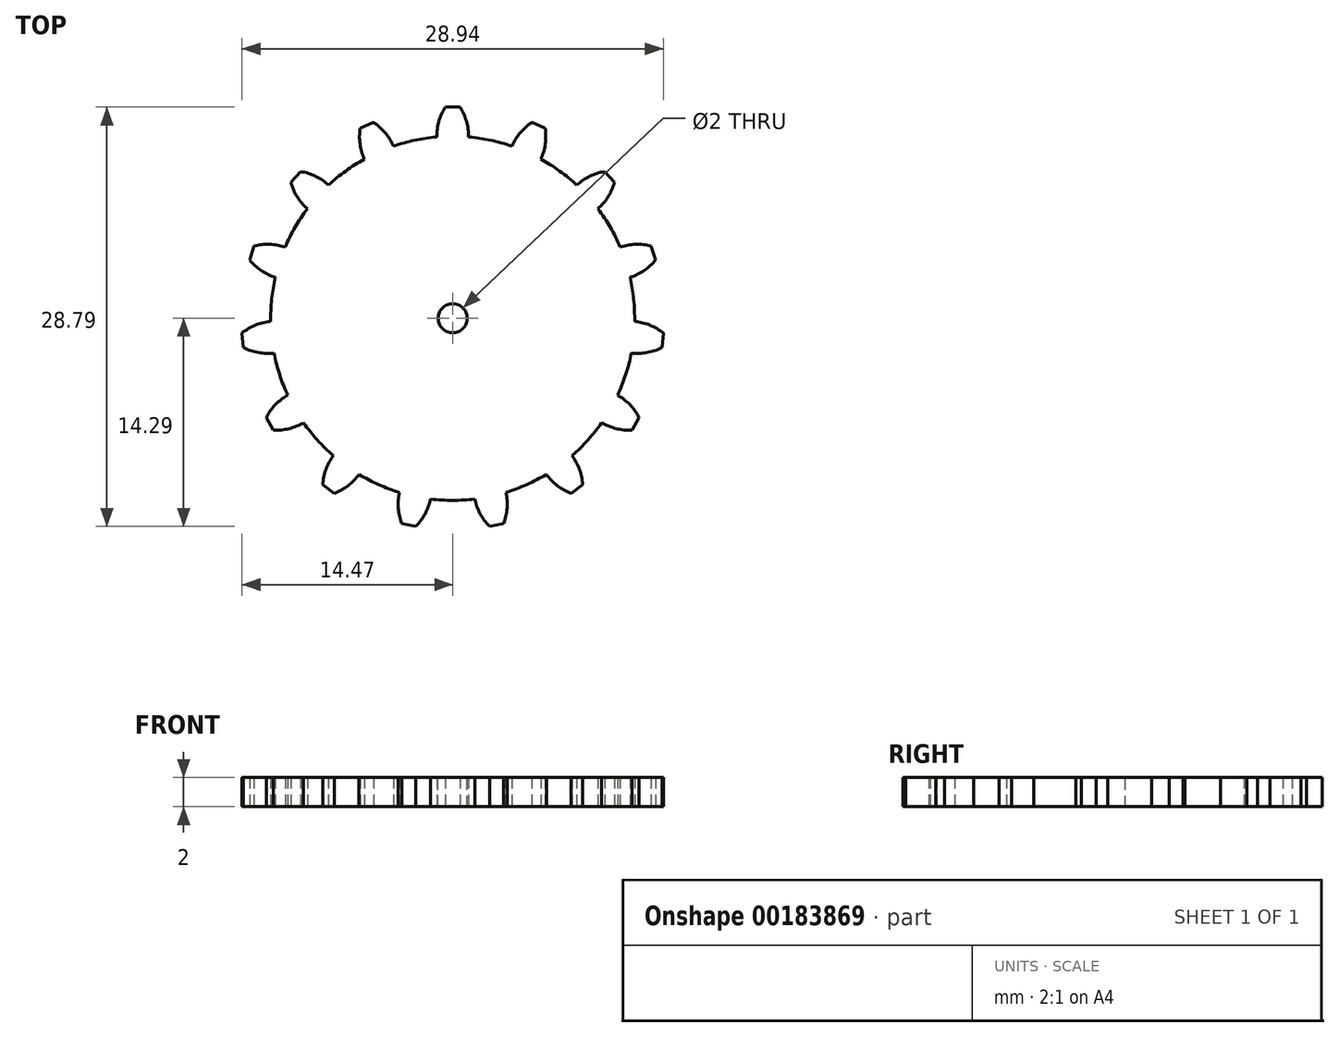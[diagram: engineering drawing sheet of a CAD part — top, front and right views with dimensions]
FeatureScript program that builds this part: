
annotation { "Feature Type Name" : "Feature", "Feature Type Description" : "" }
export const myFeature = defineFeature(function(context is Context, id is Id, definition is map)
    precondition{}
    {
        {
            var Q0;
            Q0=qCreatedBy(makeId("Top.planeOp"),FACE);
            var sketch = newSketch(context, id + "F0", { "sketchPlane" : qUnion([Q0])});
            skCircle(sketch, "E0", {"center": v(0, 0) * mm, "radius": 12.5 * mm});
            skLineSegment(sketch, "E1", {"start": v(0, 0) * mm, "end": v(0, 12.5) * mm, "construction": true});
            skLineSegment(sketch, "E2", {"start": v(0, 14.5) * mm, "end": v(-0.5, 14.5) * mm});
            skArc(sketch, "E3", {"start": v(-0.5, 14.5) * mm, "mid": v(-0.95, 13.52) * mm, "end": v(-1.09, 12.45) * mm});
            skLineSegment(sketch, "E4.MirrorCS", {"start": v(0, 14.5) * mm, "end": v(0.5, 14.5) * mm});
            skArc(sketch, "E5.MirrorCS", {"start": v(0.5, 14.5) * mm, "mid": v(0.95, 13.52) * mm, "end": v(1.09, 12.45) * mm});
            skArc(sketch, "E6.1.0", {"start": v(-6.35, 13.04) * mm, "mid": v(-6.36, 11.97) * mm, "end": v(-6.06, 10.93) * mm});
            skLineSegment(sketch, "E6.1.1", {"start": v(-5.9, 13.25) * mm, "end": v(-6.35, 13.04) * mm});
            skLineSegment(sketch, "E6.1.2", {"start": v(-5.9, 13.25) * mm, "end": v(-5.44, 13.45) * mm});
            skArc(sketch, "E6.1.3", {"start": v(-5.44, 13.45) * mm, "mid": v(-4.64, 12.74) * mm, "end": v(-4.07, 11.82) * mm});
            skArc(sketch, "E6.2.0", {"start": v(-11.11, 9.33) * mm, "mid": v(-10.68, 8.34) * mm, "end": v(-9.98, 7.52) * mm});
            skLineSegment(sketch, "E6.2.1", {"start": v(-10.78, 9.7) * mm, "end": v(-11.11, 9.33) * mm});
            skLineSegment(sketch, "E6.2.2", {"start": v(-10.78, 9.7) * mm, "end": v(-10.44, 10.07) * mm});
            skArc(sketch, "E6.2.3", {"start": v(-10.44, 10.07) * mm, "mid": v(-9.41, 9.75) * mm, "end": v(-8.53, 9.14) * mm});
            skArc(sketch, "E6.3.0", {"start": v(-13.94, 4) * mm, "mid": v(-13.15, 3.28) * mm, "end": v(-12.18, 2.81) * mm});
            skLineSegment(sketch, "E6.3.1", {"start": v(-13.8, 4.48) * mm, "end": v(-13.94, 4) * mm});
            skLineSegment(sketch, "E6.3.2", {"start": v(-13.8, 4.48) * mm, "end": v(-13.64, 4.96) * mm});
            skArc(sketch, "E6.3.3", {"start": v(-13.64, 4.96) * mm, "mid": v(-12.57, 5.08) * mm, "end": v(-11.5, 4.88) * mm});
            skArc(sketch, "E6.4.0", {"start": v(-14.37, -2.01) * mm, "mid": v(-13.35, -2.35) * mm, "end": v(-12.27, -2.38) * mm});
            skLineSegment(sketch, "E6.4.1", {"start": v(-14.42, -1.52) * mm, "end": v(-14.37, -2.01) * mm});
            skLineSegment(sketch, "E6.4.2", {"start": v(-14.42, -1.52) * mm, "end": v(-14.47, -1.02) * mm});
            skArc(sketch, "E6.4.3", {"start": v(-14.47, -1.02) * mm, "mid": v(-13.54, -0.47) * mm, "end": v(-12.5, -0.22) * mm});
            skArc(sketch, "E6.5.0", {"start": v(-12.3, -7.68) * mm, "mid": v(-11.24, -7.58) * mm, "end": v(-10.24, -7.17) * mm});
            skLineSegment(sketch, "E6.5.1", {"start": v(-12.56, -7.25) * mm, "end": v(-12.3, -7.68) * mm});
            skLineSegment(sketch, "E6.5.2", {"start": v(-12.56, -7.25) * mm, "end": v(-12.8, -6.82) * mm});
            skArc(sketch, "E6.5.3", {"start": v(-12.8, -6.82) * mm, "mid": v(-12.18, -5.94) * mm, "end": v(-11.33, -5.28) * mm});
            skArc(sketch, "E6.6.0", {"start": v(-8.12, -12.02) * mm, "mid": v(-7.18, -11.5) * mm, "end": v(-6.44, -10.71) * mm});
            skLineSegment(sketch, "E6.6.1", {"start": v(-8.52, -11.73) * mm, "end": v(-8.12, -12.02) * mm});
            skLineSegment(sketch, "E6.6.2", {"start": v(-8.52, -11.73) * mm, "end": v(-8.93, -11.44) * mm});
            skArc(sketch, "E6.6.3", {"start": v(-8.93, -11.44) * mm, "mid": v(-8.71, -10.38) * mm, "end": v(-8.2, -9.43) * mm});
            skArc(sketch, "E6.7.0", {"start": v(-2.53, -14.29) * mm, "mid": v(-1.89, -13.42) * mm, "end": v(-1.52, -12.4) * mm});
            skLineSegment(sketch, "E6.7.1", {"start": v(-3.01, -14.18) * mm, "end": v(-2.53, -14.29) * mm});
            skLineSegment(sketch, "E6.7.2", {"start": v(-3.01, -14.18) * mm, "end": v(-3.5, -14.08) * mm});
            skArc(sketch, "E6.7.3", {"start": v(-3.5, -14.08) * mm, "mid": v(-3.74, -13.03) * mm, "end": v(-3.65, -11.95) * mm});
            skArc(sketch, "E6.8.0", {"start": v(3.5, -14.08) * mm, "mid": v(3.74, -13.03) * mm, "end": v(3.65, -11.95) * mm});
            skLineSegment(sketch, "E6.8.1", {"start": v(3.01, -14.18) * mm, "end": v(3.5, -14.08) * mm});
            skLineSegment(sketch, "E6.8.2", {"start": v(3.01, -14.18) * mm, "end": v(2.53, -14.29) * mm});
            skArc(sketch, "E6.8.3", {"start": v(2.53, -14.29) * mm, "mid": v(1.89, -13.42) * mm, "end": v(1.52, -12.4) * mm});
            skArc(sketch, "E6.9.0", {"start": v(8.93, -11.44) * mm, "mid": v(8.71, -10.38) * mm, "end": v(8.2, -9.43) * mm});
            skLineSegment(sketch, "E6.9.1", {"start": v(8.52, -11.73) * mm, "end": v(8.93, -11.44) * mm});
            skLineSegment(sketch, "E6.9.2", {"start": v(8.52, -11.73) * mm, "end": v(8.12, -12.02) * mm});
            skArc(sketch, "E6.9.3", {"start": v(8.12, -12.02) * mm, "mid": v(7.18, -11.5) * mm, "end": v(6.44, -10.71) * mm});
            skArc(sketch, "E6.10.0", {"start": v(12.8, -6.82) * mm, "mid": v(12.18, -5.94) * mm, "end": v(11.33, -5.28) * mm});
            skLineSegment(sketch, "E6.10.1", {"start": v(12.56, -7.25) * mm, "end": v(12.8, -6.82) * mm});
            skLineSegment(sketch, "E6.10.2", {"start": v(12.56, -7.25) * mm, "end": v(12.3, -7.68) * mm});
            skArc(sketch, "E6.10.3", {"start": v(12.3, -7.68) * mm, "mid": v(11.24, -7.58) * mm, "end": v(10.24, -7.17) * mm});
            skArc(sketch, "E6.11.0", {"start": v(14.47, -1.02) * mm, "mid": v(13.54, -0.47) * mm, "end": v(12.5, -0.22) * mm});
            skLineSegment(sketch, "E6.11.1", {"start": v(14.42, -1.52) * mm, "end": v(14.47, -1.02) * mm});
            skLineSegment(sketch, "E6.11.2", {"start": v(14.42, -1.52) * mm, "end": v(14.37, -2.01) * mm});
            skArc(sketch, "E6.11.3", {"start": v(14.37, -2.01) * mm, "mid": v(13.35, -2.35) * mm, "end": v(12.27, -2.38) * mm});
            skArc(sketch, "E6.12.0", {"start": v(13.64, 4.96) * mm, "mid": v(12.57, 5.08) * mm, "end": v(11.5, 4.88) * mm});
            skLineSegment(sketch, "E6.12.1", {"start": v(13.8, 4.48) * mm, "end": v(13.64, 4.96) * mm});
            skLineSegment(sketch, "E6.12.2", {"start": v(13.8, 4.48) * mm, "end": v(13.94, 4) * mm});
            skArc(sketch, "E6.12.3", {"start": v(13.94, 4) * mm, "mid": v(13.15, 3.28) * mm, "end": v(12.18, 2.81) * mm});
            skArc(sketch, "E6.13.0", {"start": v(10.44, 10.07) * mm, "mid": v(9.41, 9.75) * mm, "end": v(8.53, 9.14) * mm});
            skLineSegment(sketch, "E6.13.1", {"start": v(10.78, 9.7) * mm, "end": v(10.44, 10.07) * mm});
            skLineSegment(sketch, "E6.13.2", {"start": v(10.78, 9.7) * mm, "end": v(11.11, 9.33) * mm});
            skArc(sketch, "E6.13.3", {"start": v(11.11, 9.33) * mm, "mid": v(10.68, 8.34) * mm, "end": v(9.98, 7.52) * mm});
            skArc(sketch, "E6.14.0", {"start": v(5.44, 13.45) * mm, "mid": v(4.64, 12.74) * mm, "end": v(4.07, 11.82) * mm});
            skLineSegment(sketch, "E6.14.1", {"start": v(5.9, 13.25) * mm, "end": v(5.44, 13.45) * mm});
            skLineSegment(sketch, "E6.14.2", {"start": v(5.9, 13.25) * mm, "end": v(6.35, 13.04) * mm});
            skArc(sketch, "E6.14.3", {"start": v(6.35, 13.04) * mm, "mid": v(6.36, 11.97) * mm, "end": v(6.06, 10.93) * mm});
            skSolve(sketch);
        }
        {
            var Q0;
            Q0=qSketchRegion(id+"F0",true);
            extrude(context, id + "F1", {"entities" : qUnion([Q0]), "depth" : 2 * mm});
        }
        {
            var Q0;
            Q0=makeQuery(id+"F1.opExtrude","CAP_FACE",FACE,{"disambiguationData":[OSD([sQuery(id+"F0.wireOp",EDGE,"E0"),sQuery(id+"F0.wireOp",EDGE,"E2"),sQuery(id+"F0.wireOp",EDGE,"E3"),sQuery(id+"F0.wireOp",EDGE,"E4.MirrorCS"),sQuery(id+"F0.wireOp",EDGE,"E5.MirrorCS"),sQuery(id+"F0.wireOp",EDGE,"E6.1.0"),sQuery(id+"F0.wireOp",EDGE,"E6.1.1"),sQuery(id+"F0.wireOp",EDGE,"E6.1.2"),sQuery(id+"F0.wireOp",EDGE,"E6.1.3"),sQuery(id+"F0.wireOp",EDGE,"E6.2.0"),sQuery(id+"F0.wireOp",EDGE,"E6.2.1"),sQuery(id+"F0.wireOp",EDGE,"E6.2.2"),sQuery(id+"F0.wireOp",EDGE,"E6.2.3"),sQuery(id+"F0.wireOp",EDGE,"E6.3.0"),sQuery(id+"F0.wireOp",EDGE,"E6.3.1"),sQuery(id+"F0.wireOp",EDGE,"E6.3.2"),sQuery(id+"F0.wireOp",EDGE,"E6.3.3"),sQuery(id+"F0.wireOp",EDGE,"E6.4.0"),sQuery(id+"F0.wireOp",EDGE,"E6.4.1"),sQuery(id+"F0.wireOp",EDGE,"E6.4.2"),sQuery(id+"F0.wireOp",EDGE,"E6.4.3"),sQuery(id+"F0.wireOp",EDGE,"E6.5.0"),sQuery(id+"F0.wireOp",EDGE,"E6.5.1"),sQuery(id+"F0.wireOp",EDGE,"E6.5.2"),sQuery(id+"F0.wireOp",EDGE,"E6.5.3"),sQuery(id+"F0.wireOp",EDGE,"E6.6.0"),sQuery(id+"F0.wireOp",EDGE,"E6.6.1"),sQuery(id+"F0.wireOp",EDGE,"E6.6.2"),sQuery(id+"F0.wireOp",EDGE,"E6.6.3"),sQuery(id+"F0.wireOp",EDGE,"E6.7.0"),sQuery(id+"F0.wireOp",EDGE,"E6.7.1"),sQuery(id+"F0.wireOp",EDGE,"E6.7.2"),sQuery(id+"F0.wireOp",EDGE,"E6.7.3"),sQuery(id+"F0.wireOp",EDGE,"E6.8.0"),sQuery(id+"F0.wireOp",EDGE,"E6.8.1"),sQuery(id+"F0.wireOp",EDGE,"E6.8.2"),sQuery(id+"F0.wireOp",EDGE,"E6.8.3"),sQuery(id+"F0.wireOp",EDGE,"E6.9.0"),sQuery(id+"F0.wireOp",EDGE,"E6.9.1"),sQuery(id+"F0.wireOp",EDGE,"E6.9.2"),sQuery(id+"F0.wireOp",EDGE,"E6.9.3"),sQuery(id+"F0.wireOp",EDGE,"E6.10.0"),sQuery(id+"F0.wireOp",EDGE,"E6.10.1"),sQuery(id+"F0.wireOp",EDGE,"E6.10.2"),sQuery(id+"F0.wireOp",EDGE,"E6.10.3"),sQuery(id+"F0.wireOp",EDGE,"E6.11.0"),sQuery(id+"F0.wireOp",EDGE,"E6.11.1"),sQuery(id+"F0.wireOp",EDGE,"E6.11.2"),sQuery(id+"F0.wireOp",EDGE,"E6.11.3"),sQuery(id+"F0.wireOp",EDGE,"E6.12.0"),sQuery(id+"F0.wireOp",EDGE,"E6.12.1"),sQuery(id+"F0.wireOp",EDGE,"E6.12.2"),sQuery(id+"F0.wireOp",EDGE,"E6.12.3"),sQuery(id+"F0.wireOp",EDGE,"E6.13.0"),sQuery(id+"F0.wireOp",EDGE,"E6.13.1"),sQuery(id+"F0.wireOp",EDGE,"E6.13.2"),sQuery(id+"F0.wireOp",EDGE,"E6.13.3"),sQuery(id+"F0.wireOp",EDGE,"E6.14.0"),sQuery(id+"F0.wireOp",EDGE,"E6.14.1"),sQuery(id+"F0.wireOp",EDGE,"E6.14.2"),sQuery(id+"F0.wireOp",EDGE,"E6.14.3")])],"isStart":false});
            var sketch = newSketch(context, id + "F2", { "sketchPlane" : qUnion([Q0])});
            skCircle(sketch, "E7", {"center": v(0, 0) * mm, "radius": 1 * mm});
            skSolve(sketch);
        }
        {
            var Q0;
            Q0=makeQuery(id+"F2.imprint","IMPRINT",FACE,{"disambiguationData":[TD([[makeQuery(id+"F2.imprint","IMPRINT",EDGE,{"derivedFrom":sQuery(id+"F2.wireOp",EDGE,"E7")}),1.0]])]});
            extrude(context, id + "F3", {"entities" : qUnion([Q0]), "operationType" : NewBodyOperationType.REMOVE, "endBound" : BoundingType.THROUGH_ALL, "oppositeDirection" : true, "depth" : 25 * mm});
        }
    });
